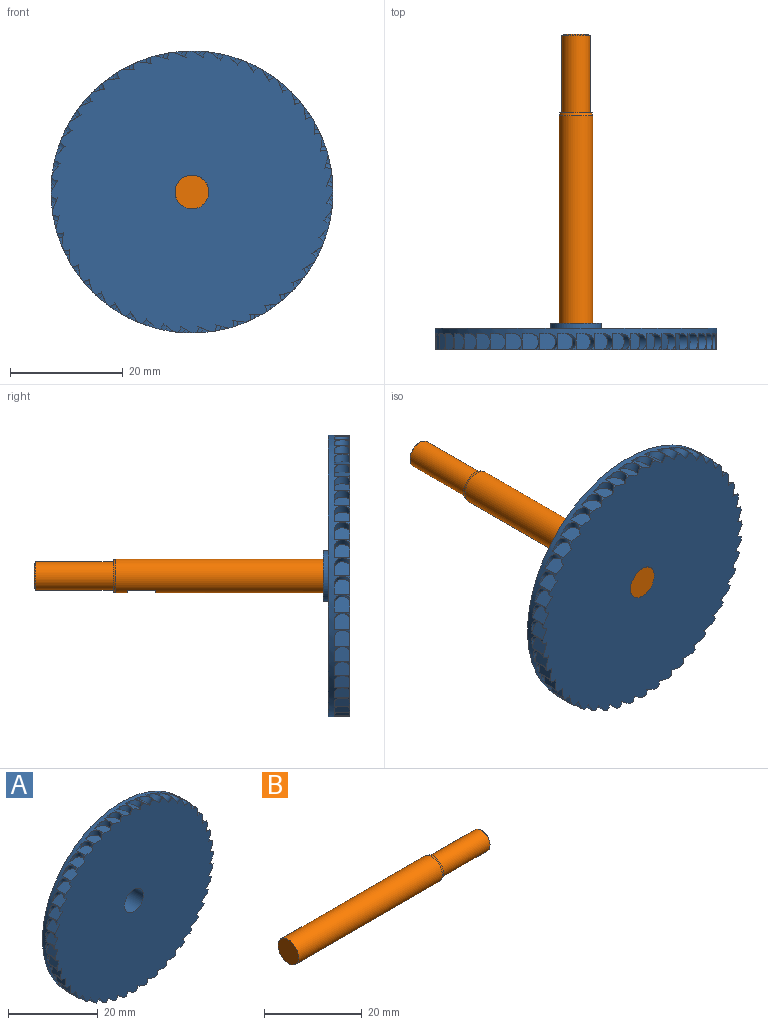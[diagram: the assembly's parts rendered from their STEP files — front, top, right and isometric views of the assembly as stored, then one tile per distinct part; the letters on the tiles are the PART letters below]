
ASSEMBLY  parts=2 mates=2
PART A: 150 faces, bbox 51.1x4.7x51.1 mm
  f0: cylinder r=1.5mm len=2.8mm, axis (0,0,-1), area 4.9mm2, adj f48,f49,f98,f146
  f1: cylinder r=1.5mm len=2.8mm, axis (0.13,0,-0.99), area 4.9mm2, adj f49,f50,f99,f146
  f2: cylinder r=1.5mm len=2.8mm, axis (0.26,0,-0.97), area 4.9mm2, adj f49,f51,f100,f146
  f3: cylinder r=1.5mm len=2.8mm, axis (0.38,0,-0.92), area 4.9mm2, adj f49,f52,f101,f146
  f4: cylinder r=1.5mm len=2.8mm, axis (0.5,0,-0.87), area 4.9mm2, adj f49,f53,f102,f146
  f5: cylinder r=1.5mm len=2.8mm, axis (0.61,0,-0.79), area 4.9mm2, adj f49,f54,f103,f146
  f6: cylinder r=1.5mm len=2.8mm, axis (0.71,0,-0.71), area 4.9mm2, adj f49,f55,f104,f146
  f7: cylinder r=1.5mm len=2.8mm, axis (0.79,0,-0.61), area 4.9mm2, adj f49,f56,f105,f146
  f8: cylinder r=1.5mm len=2.8mm, axis (0.87,0,-0.5), area 4.9mm2, adj f49,f57,f106,f146
  f9: cylinder r=1.5mm len=2.8mm, axis (0.92,0,-0.38), area 4.9mm2, adj f49,f58,f107,f146
  f10: cylinder r=1.5mm len=2.8mm, axis (0.97,0,-0.26), area 4.9mm2, adj f49,f59,f108,f146
  f11: cylinder r=1.5mm len=2.8mm, axis (0.99,0,-0.13), area 4.9mm2, adj f49,f60,f109,f146
  f12: cylinder r=1.5mm len=2.8mm, axis (1,0,0), area 4.9mm2, adj f49,f61,f110,f146
  f13: cylinder r=1.5mm len=2.8mm, axis (0.99,0,0.13), area 4.9mm2, adj f49,f62,f111,f146
  f14: cylinder r=1.5mm len=2.8mm, axis (0.97,0,0.26), area 4.9mm2, adj f49,f63,f112,f146
  f15: cylinder r=1.5mm len=2.8mm, axis (0.92,0,0.38), area 4.9mm2, adj f49,f64,f113,f146
  f16: cylinder r=1.5mm len=2.8mm, axis (0.87,0,0.5), area 4.9mm2, adj f49,f65,f114,f146
  f17: cylinder r=1.5mm len=2.8mm, axis (0.79,0,0.61), area 4.9mm2, adj f49,f66,f115,f146
  f18: cylinder r=1.5mm len=2.8mm, axis (0.71,0,0.71), area 4.9mm2, adj f49,f67,f116,f146
  f19: cylinder r=1.5mm len=2.8mm, axis (0.61,0,0.79), area 4.9mm2, adj f49,f68,f117,f146
  f20: cylinder r=1.5mm len=2.8mm, axis (0.5,0,0.87), area 4.9mm2, adj f49,f69,f118,f146
  f21: cylinder r=1.5mm len=2.8mm, axis (0.38,0,0.92), area 4.9mm2, adj f49,f70,f119,f146
  f22: cylinder r=1.5mm len=2.8mm, axis (0.26,0,0.97), area 4.9mm2, adj f49,f71,f120,f146
  f23: cylinder r=1.5mm len=2.8mm, axis (0.13,0,0.99), area 4.9mm2, adj f49,f72,f121,f146
  f24: cylinder r=1.5mm len=2.8mm, axis (0,0,1), area 4.9mm2, adj f49,f73,f122,f146
  f25: cylinder r=1.5mm len=2.8mm, axis (-0.13,0,0.99), area 4.9mm2, adj f49,f74,f123,f146
  f26: cylinder r=1.5mm len=2.8mm, axis (-0.26,0,0.97), area 4.9mm2, adj f49,f75,f124,f146
  f27: cylinder r=1.5mm len=2.8mm, axis (-0.38,0,0.92), area 4.9mm2, adj f49,f76,f125,f146
  f28: cylinder r=1.5mm len=2.8mm, axis (-0.5,0,0.87), area 4.9mm2, adj f49,f77,f126,f146
  f29: cylinder r=1.5mm len=2.8mm, axis (-0.61,0,0.79), area 4.9mm2, adj f49,f78,f127,f146
  f30: cylinder r=1.5mm len=2.8mm, axis (-0.71,0,0.71), area 4.9mm2, adj f49,f79,f128,f146
  f31: cylinder r=1.5mm len=2.8mm, axis (-0.79,0,0.61), area 4.9mm2, adj f49,f80,f129,f146
  f32: cylinder r=1.5mm len=2.8mm, axis (-0.87,0,0.5), area 4.9mm2, adj f49,f81,f130,f146
  f33: cylinder r=1.5mm len=2.8mm, axis (-0.92,0,0.38), area 4.9mm2, adj f49,f82,f131,f146
  f34: cylinder r=1.5mm len=2.8mm, axis (-0.97,0,0.26), area 4.9mm2, adj f49,f83,f132,f146
  f35: cylinder r=1.5mm len=2.8mm, axis (-0.99,0,0.13), area 4.9mm2, adj f49,f84,f133,f146
  f36: cylinder r=1.5mm len=2.8mm, axis (-1,0,0), area 4.9mm2, adj f49,f85,f134,f146
  f37: cylinder r=1.5mm len=2.8mm, axis (-0.99,0,-0.13), area 4.9mm2, adj f49,f86,f135,f146
  f38: cylinder r=1.5mm len=2.8mm, axis (-0.97,0,-0.26), area 4.9mm2, adj f49,f87,f136,f146
  f39: cylinder r=1.5mm len=2.8mm, axis (-0.92,0,-0.38), area 4.9mm2, adj f49,f88,f137,f146
  f40: cylinder r=1.5mm len=2.8mm, axis (-0.87,0,-0.5), area 4.9mm2, adj f49,f89,f138,f146
  f41: cylinder r=1.5mm len=2.8mm, axis (-0.79,0,-0.61), area 4.9mm2, adj f49,f90,f139,f146
  f42: cylinder r=1.5mm len=2.8mm, axis (-0.71,0,-0.71), area 4.9mm2, adj f49,f91,f140,f146
  f43: cylinder r=1.5mm len=2.8mm, axis (-0.61,0,-0.79), area 4.9mm2, adj f49,f92,f141,f146
  f44: cylinder r=1.5mm len=2.8mm, axis (-0.5,0,-0.87), area 4.9mm2, adj f49,f93,f142,f146
  f45: cylinder r=1.5mm len=2.8mm, axis (-0.38,0,-0.92), area 4.9mm2, adj f49,f94,f143,f146
  f46: cylinder r=1.5mm len=2.8mm, axis (-0.26,0,-0.97), area 4.9mm2, adj f49,f95,f144,f146
  f47: cylinder r=1.5mm len=2.8mm, axis (-0.13,0,-0.99), area 4.9mm2, adj f49,f96,f145,f146
  f48: plane 2.9x2.8mm, normal (0,0,1), area 7.4mm2, adj f0,f49,f98,f146
  f49: cylinder r=25mm len=50mm, axis (0,-1,0), area 202.3mm2, adj f0,f1,f2,f3,f4,f5,f6,f7
  f50: plane 2.88x2.8mm, normal (-0.13,0,0.99), area 7.4mm2, adj f1,f49,f99,f146
  f51: plane 2.8x2.8mm, normal (-0.26,0,0.97), area 7.4mm2, adj f2,f49,f100,f146
  f52: plane 2.8x2.68mm, normal (-0.38,0,0.92), area 7.4mm2, adj f3,f49,f101,f146
  f53: plane 2.8x2.51mm, normal (-0.5,0,0.87), area 7.4mm2, adj f4,f49,f102,f146
  f54: plane 2.8x2.3mm, normal (-0.61,0,0.79), area 7.4mm2, adj f5,f49,f103,f146
  f55: plane 2.8x2.05mm, normal (-0.71,0,0.71), area 7.4mm2, adj f6,f49,f104,f146
  f56: plane 2.8x2.3mm, normal (-0.79,0,0.61), area 7.4mm2, adj f7,f49,f105,f146
  f57: plane 2.8x2.51mm, normal (-0.87,0,0.5), area 7.4mm2, adj f8,f49,f106,f146
  f58: plane 2.8x2.68mm, normal (-0.92,0,0.38), area 7.4mm2, adj f9,f49,f107,f146
  f59: plane 2.8x2.8mm, normal (-0.97,0,0.26), area 7.4mm2, adj f10,f49,f108,f146
  f60: plane 2.88x2.8mm, normal (-0.99,0,0.13), area 7.4mm2, adj f11,f49,f109,f146
  f61: plane 2.9x2.8mm, normal (-1,0,0), area 7.4mm2, adj f12,f49,f110,f146
  f62: plane 2.88x2.8mm, normal (-0.99,0,-0.13), area 7.4mm2, adj f13,f49,f111,f146
  f63: plane 2.8x2.8mm, normal (-0.97,0,-0.26), area 7.4mm2, adj f14,f49,f112,f146
  f64: plane 2.8x2.68mm, normal (-0.92,0,-0.38), area 7.4mm2, adj f15,f49,f113,f146
  f65: plane 2.8x2.51mm, normal (-0.87,0,-0.5), area 7.4mm2, adj f16,f49,f114,f146
  f66: plane 2.8x2.3mm, normal (-0.79,0,-0.61), area 7.4mm2, adj f17,f49,f115,f146
  f67: plane 2.8x2.05mm, normal (-0.71,0,-0.71), area 7.4mm2, adj f18,f49,f116,f146
  f68: plane 2.8x2.3mm, normal (-0.61,0,-0.79), area 7.4mm2, adj f19,f49,f117,f146
  f69: plane 2.8x2.51mm, normal (-0.5,0,-0.87), area 7.4mm2, adj f20,f49,f118,f146
  f70: plane 2.8x2.68mm, normal (-0.38,0,-0.92), area 7.4mm2, adj f21,f49,f119,f146
  f71: plane 2.8x2.8mm, normal (-0.26,0,-0.97), area 7.4mm2, adj f22,f49,f120,f146
  f72: plane 2.88x2.8mm, normal (-0.13,0,-0.99), area 7.4mm2, adj f23,f49,f121,f146
  f73: plane 2.9x2.8mm, normal (0,0,-1), area 7.4mm2, adj f24,f49,f122,f146
  f74: plane 2.88x2.8mm, normal (0.13,0,-0.99), area 7.4mm2, adj f25,f49,f123,f146
  f75: plane 2.8x2.8mm, normal (0.26,0,-0.97), area 7.4mm2, adj f26,f49,f124,f146
  f76: plane 2.8x2.68mm, normal (0.38,0,-0.92), area 7.4mm2, adj f27,f49,f125,f146
  f77: plane 2.8x2.51mm, normal (0.5,0,-0.87), area 7.4mm2, adj f28,f49,f126,f146
  f78: plane 2.8x2.3mm, normal (0.61,0,-0.79), area 7.4mm2, adj f29,f49,f127,f146
  f79: plane 2.8x2.05mm, normal (0.71,0,-0.71), area 7.4mm2, adj f30,f49,f128,f146
  f80: plane 2.8x2.3mm, normal (0.79,0,-0.61), area 7.4mm2, adj f31,f49,f129,f146
  f81: plane 2.8x2.51mm, normal (0.87,0,-0.5), area 7.4mm2, adj f32,f49,f130,f146
  f82: plane 2.8x2.68mm, normal (0.92,0,-0.38), area 7.4mm2, adj f33,f49,f131,f146
  f83: plane 2.8x2.8mm, normal (0.97,0,-0.26), area 7.4mm2, adj f34,f49,f132,f146
  f84: plane 2.88x2.8mm, normal (0.99,0,-0.13), area 7.4mm2, adj f35,f49,f133,f146
  f85: plane 2.9x2.8mm, normal (1,0,0), area 7.4mm2, adj f36,f49,f134,f146
  f86: plane 2.88x2.8mm, normal (0.99,0,0.13), area 7.4mm2, adj f37,f49,f135,f146
  f87: plane 2.8x2.8mm, normal (0.97,0,0.26), area 7.4mm2, adj f38,f49,f136,f146
  f88: plane 2.8x2.68mm, normal (0.92,0,0.38), area 7.4mm2, adj f39,f49,f137,f146
  f89: plane 2.8x2.51mm, normal (0.87,0,0.5), area 7.4mm2, adj f40,f49,f138,f146
  f90: plane 2.8x2.3mm, normal (0.79,0,0.61), area 7.4mm2, adj f41,f49,f139,f146
  f91: plane 2.8x2.05mm, normal (0.71,0,0.71), area 7.4mm2, adj f42,f49,f140,f146
  f92: plane 2.8x2.3mm, normal (0.61,0,0.79), area 7.4mm2, adj f43,f49,f141,f146
  f93: plane 2.8x2.51mm, normal (0.5,0,0.87), area 7.4mm2, adj f44,f49,f142,f146
  f94: plane 2.8x2.68mm, normal (0.38,0,0.92), area 7.4mm2, adj f45,f49,f143,f146
  f95: plane 2.8x2.8mm, normal (0.26,0,0.97), area 7.4mm2, adj f46,f49,f144,f146
  f96: plane 2.88x2.8mm, normal (0.13,0,0.99), area 7.4mm2, adj f47,f49,f145,f146
  f97: plane 50x50mm, normal (0,1,0), area 1899.9mm2, adj f49,f147
  f98: plane 1.4x0.75mm, normal (0,-1,0), area 0.5mm2, adj f0,f48,f49
  f99: plane 1.39x0.93mm, normal (0,-1,0), area 0.5mm2, adj f1,f49,f50
  f100: plane 1.35x1.09mm, normal (0,-1,0), area 0.5mm2, adj f2,f49,f51
  f101: plane 1.29x1.23mm, normal (0,-1,0), area 0.5mm2, adj f3,f49,f52
  f102: plane 1.35x1.21mm, normal (0,-1,0), area 0.5mm2, adj f4,f49,f53
  f103: plane 1.45x1.11mm, normal (0,-1,0), area 0.5mm2, adj f5,f49,f54
  f104: plane 1.52x0.99mm, normal (0,-1,0), area 0.5mm2, adj f6,f49,f55
  f105: plane 1.57x0.85mm, normal (0,-1,0), area 0.5mm2, adj f7,f49,f56
  f106: plane 1.59x0.7mm, normal (0,-1,0), area 0.5mm2, adj f8,f49,f57
  f107: plane 1.58x0.69mm, normal (0,-1,0), area 0.5mm2, adj f9,f49,f58
  f108: plane 1.55x0.72mm, normal (0,-1,0), area 0.5mm2, adj f10,f49,f59
  f109: plane 1.49x0.74mm, normal (0,-1,0), area 0.5mm2, adj f11,f49,f60
  f110: plane 1.4x0.75mm, normal (0,-1,0), area 0.5mm2, adj f12,f49,f61
  f111: plane 1.39x0.93mm, normal (0,-1,0), area 0.5mm2, adj f13,f49,f62
  f112: plane 1.35x1.09mm, normal (0,-1,0), area 0.5mm2, adj f14,f49,f63
  f113: plane 1.29x1.23mm, normal (0,-1,0), area 0.5mm2, adj f15,f49,f64
  f114: plane 1.35x1.21mm, normal (0,-1,0), area 0.5mm2, adj f16,f49,f65
  f115: plane 1.45x1.11mm, normal (0,-1,0), area 0.5mm2, adj f17,f49,f66
  f116: plane 1.52x0.99mm, normal (0,-1,0), area 0.5mm2, adj f18,f49,f67
  f117: plane 1.57x0.85mm, normal (0,-1,0), area 0.5mm2, adj f19,f49,f68
  f118: plane 1.59x0.7mm, normal (0,-1,0), area 0.5mm2, adj f20,f49,f69
  f119: plane 1.58x0.69mm, normal (0,-1,0), area 0.5mm2, adj f21,f49,f70
  f120: plane 1.55x0.72mm, normal (0,-1,0), area 0.5mm2, adj f22,f49,f71
  f121: plane 1.49x0.74mm, normal (0,-1,0), area 0.5mm2, adj f23,f49,f72
  f122: plane 1.4x0.75mm, normal (0,-1,0), area 0.5mm2, adj f24,f49,f73
  f123: plane 1.39x0.93mm, normal (0,-1,0), area 0.5mm2, adj f25,f49,f74
  f124: plane 1.35x1.09mm, normal (0,-1,0), area 0.5mm2, adj f26,f49,f75
  f125: plane 1.29x1.23mm, normal (0,-1,0), area 0.5mm2, adj f27,f49,f76
  f126: plane 1.35x1.21mm, normal (0,-1,0), area 0.5mm2, adj f28,f49,f77
  f127: plane 1.45x1.11mm, normal (0,-1,0), area 0.5mm2, adj f29,f49,f78
  f128: plane 1.52x0.99mm, normal (0,-1,0), area 0.5mm2, adj f30,f49,f79
  f129: plane 1.57x0.85mm, normal (0,-1,0), area 0.5mm2, adj f31,f49,f80
  f130: plane 1.59x0.7mm, normal (0,-1,0), area 0.5mm2, adj f32,f49,f81
  f131: plane 1.58x0.69mm, normal (0,-1,0), area 0.5mm2, adj f33,f49,f82
  f132: plane 1.55x0.72mm, normal (0,-1,0), area 0.5mm2, adj f34,f49,f83
  f133: plane 1.49x0.74mm, normal (0,-1,0), area 0.5mm2, adj f35,f49,f84
  f134: plane 1.4x0.75mm, normal (0,-1,0), area 0.5mm2, adj f36,f49,f85
  f135: plane 1.39x0.93mm, normal (0,-1,0), area 0.5mm2, adj f37,f49,f86
  f136: plane 1.35x1.09mm, normal (0,-1,0), area 0.5mm2, adj f38,f49,f87
  f137: plane 1.29x1.23mm, normal (0,-1,0), area 0.5mm2, adj f39,f49,f88
  f138: plane 1.35x1.21mm, normal (0,-1,0), area 0.5mm2, adj f40,f49,f89
  f139: plane 1.45x1.11mm, normal (0,-1,0), area 0.5mm2, adj f41,f49,f90
  f140: plane 1.52x0.99mm, normal (0,-1,0), area 0.5mm2, adj f42,f49,f91
  f141: plane 1.57x0.85mm, normal (0,-1,0), area 0.5mm2, adj f43,f49,f92
  f142: plane 1.59x0.7mm, normal (0,-1,0), area 0.5mm2, adj f44,f49,f93
  f143: plane 1.58x0.69mm, normal (0,-1,0), area 0.5mm2, adj f45,f49,f94
  f144: plane 1.55x0.72mm, normal (0,-1,0), area 0.5mm2, adj f46,f49,f95
  f145: plane 1.49x0.74mm, normal (0,-1,0), area 0.5mm2, adj f47,f49,f96
  f146: plane 50x50mm, normal (0,-1,0), area 1876mm2, adj f0,f1,f2,f3,f4,f5,f6,f7
  f147: cylinder r=4.5mm len=9mm, axis (0,-1,0), area 25.2mm2, adj f97,f148
  f148: plane 9x9mm, normal (0,1,0), area 35.3mm2, adj f147,f149
  f149: cylinder r=3mm len=6mm, axis (0,1,0), area 88.4mm2, adj f146,f148
PART B: 10 faces, bbox 56x6x6 mm
  f0: plane 5.73x5.73mm, normal (1,0,0), area 6.1mm2, adj f1,f7
  f1: cone r=3mm half-angle=15deg, axis (-1,0,0), area 9.5mm2, adj f0,f2
  f2: cylinder r=3mm len=41.49mm, axis (1,0,0), area 763.7mm2, adj f1,f3,f4,f5,f6
  f3: plane 5.99x5.99mm, normal (-1,0,0), area 28.2mm2, adj f2
  f4: plane 3.3x0.5mm, normal (1,0,0), area 1.1mm2, adj f2,f6
  f5: plane 3.3x0.5mm, normal (-1,0,0), area 1.1mm2, adj f2,f6
  f6: plane 5x3.3mm, normal (0,1,0), area 16.5mm2, adj f2,f4,f5
  f7: cylinder r=2.5mm len=13.8mm, axis (-1,0,0), area 216.8mm2, adj f0,f9
  f8: plane 4.6x4.6mm, normal (1,0,0), area 16.6mm2, adj f9
  f9: cone r=2.3mm half-angle=45deg, axis (-1,0,0), area 4.3mm2, adj f7,f8
PLACE A rot(axis=(0,1,0),7.5deg) t=(0,-1.2,0)mm
PLACE B rot(axis=(-0.58,-0.58,0.58),120deg) t=(0,0,0)mm
MATE revolute B.f1 <-> A.f49  axis (0,-1,0) through (0,0,0)mm
MATE parallel A.f50 <-> B.f6  axis (0,0,1) through (-11.15,1.37,21.66)mm
